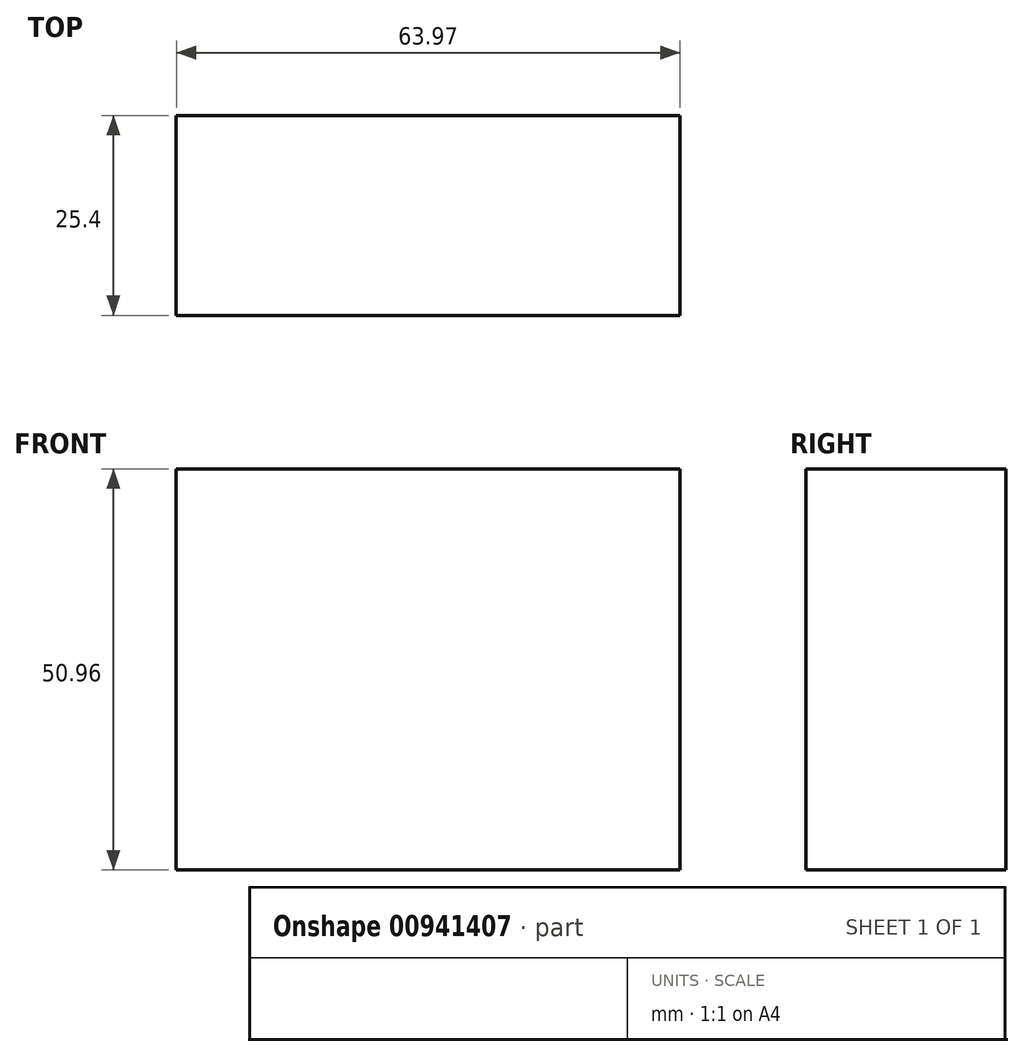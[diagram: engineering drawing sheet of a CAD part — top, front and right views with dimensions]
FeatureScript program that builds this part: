
annotation { "Feature Type Name" : "Feature", "Feature Type Description" : "" }
export const myFeature = defineFeature(function(context is Context, id is Id, definition is map)
    precondition{}
    {
        {
            var Q0;
            Q0=qCreatedBy(makeId("Front.planeOp"),FACE);
            var sketch = newSketch(context, id + "F0", { "sketchPlane" : qUnion([Q0])});
            skLineSegment(sketch, "E0.bottom", {"start": v(-40.7, 25.11) * mm, "end": v(23.28, 25.11) * mm});
            skLineSegment(sketch, "E0.top", {"start": v(-40.7, -25.85) * mm, "end": v(23.28, -25.85) * mm});
            skLineSegment(sketch, "E0.left", {"start": v(-40.7, 25.11) * mm, "end": v(-40.7, -25.85) * mm});
            skLineSegment(sketch, "E0.right", {"start": v(23.28, 25.11) * mm, "end": v(23.28, -25.85) * mm});
            skSolve(sketch);
        }
        {
            var Q0;
            Q0 = qSketchRegion(id + "F0", true);
            var sketch = newSketch(context, id + "F1", { "sketchPlane" : qUnion([Q0])});
            skLineSegment(sketch, "E1.0", {"start": v(-40.7, 25.11) * mm, "end": v(-40.7, -25.85) * mm});
            skSolve(sketch);
        }
        {
            var Q0;
            Q0 = qSketchRegion(id + "F0", true);
            extrude(context, id + "F2", {"entities" : qUnion([Q0]), "depth" : 25.4 * mm, "offsetDistance" : 25.4 * mm});
        }
    });
